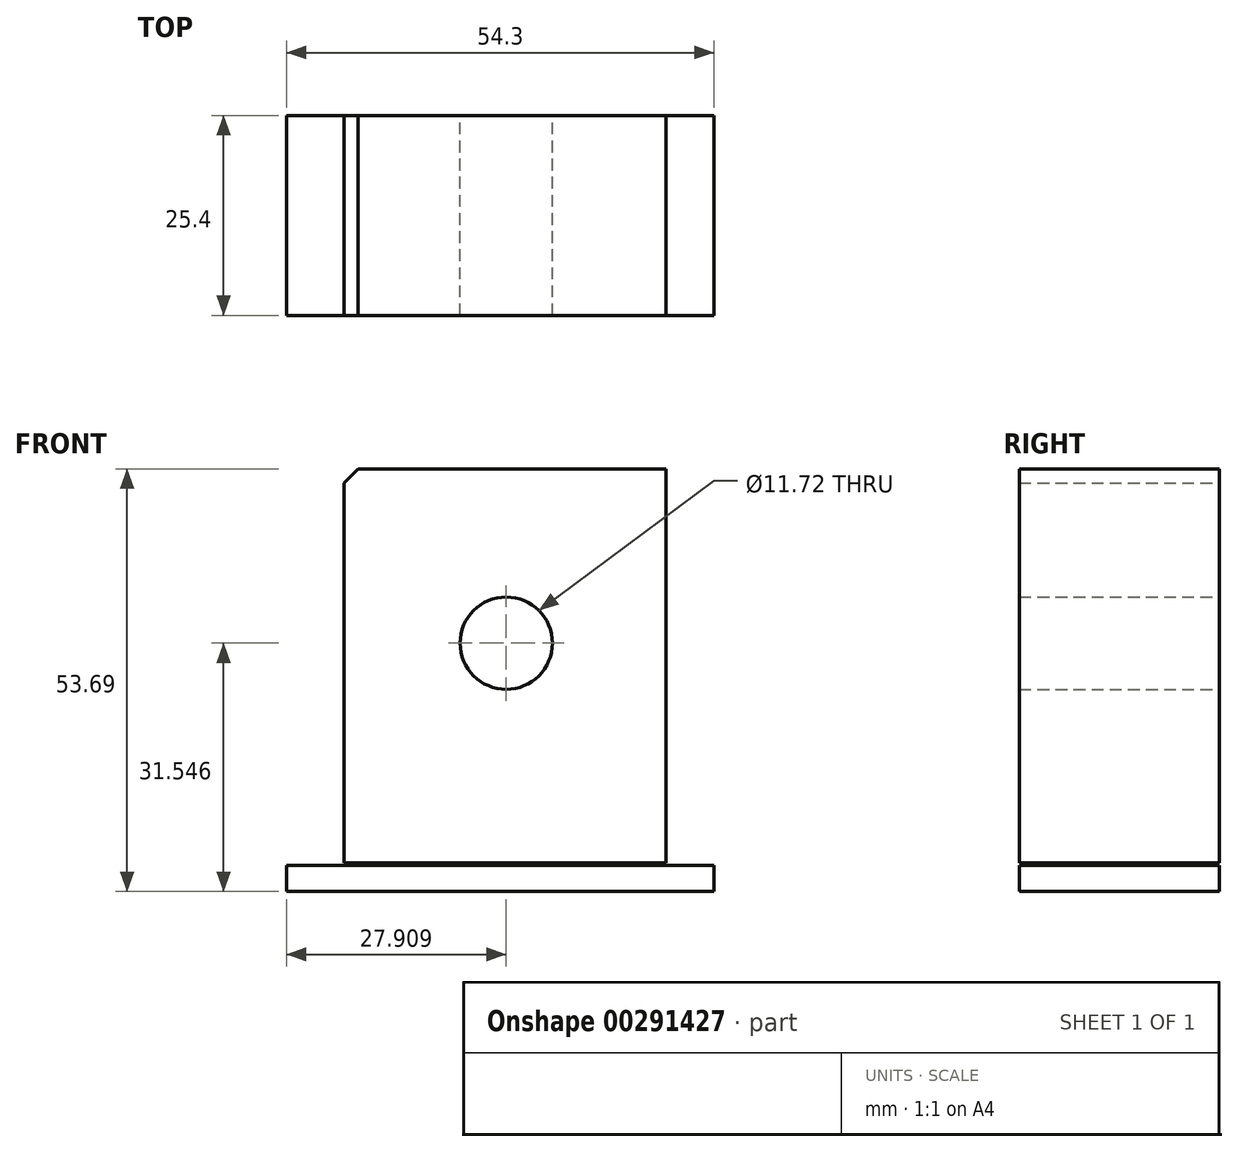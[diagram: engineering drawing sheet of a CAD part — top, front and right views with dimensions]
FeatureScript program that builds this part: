
annotation { "Feature Type Name" : "Feature", "Feature Type Description" : "" }
export const myFeature = defineFeature(function(context is Context, id is Id, definition is map)
    precondition{}
    {
        {
            var Q0;
            Q0=qCreatedBy(makeId("Front.planeOp"),FACE);
            var sketch = newSketch(context, id + "F0", { "sketchPlane" : qUnion([Q0])});
            skLineSegment(sketch, "E0.bottom", {"start": v(-24, 17.35) * mm, "end": v(16.95, 17.35) * mm});
            skLineSegment(sketch, "E0.top", {"start": v(-24, -32.7) * mm, "end": v(16.95, -32.7) * mm});
            skLineSegment(sketch, "E0.left", {"start": v(-24, 17.35) * mm, "end": v(-24, -32.7) * mm});
            skLineSegment(sketch, "E0.right", {"start": v(16.95, 17.35) * mm, "end": v(16.95, -32.7) * mm});
            skLineSegment(sketch, "E1.bottom", {"start": v(-31.28, -33) * mm, "end": v(23.02, -33) * mm});
            skLineSegment(sketch, "E1.top", {"start": v(-31.28, -36.34) * mm, "end": v(23.02, -36.34) * mm});
            skLineSegment(sketch, "E1.left", {"start": v(-31.28, -33) * mm, "end": v(-31.28, -36.34) * mm});
            skLineSegment(sketch, "E1.right", {"start": v(23.02, -33) * mm, "end": v(23.02, -36.34) * mm});
            skLineSegment(sketch, "E2", {"start": v(-39.16, 0) * mm, "end": v(0, 40.1) * mm});
            skLineSegment(sketch, "E3", {"start": v(0, 40.1) * mm, "end": v(31.2, 0) * mm});
            skCircle(sketch, "E4", {"center": v(-3.37, -4.8) * mm, "radius": 5.86 * mm});
            skCircle(sketch, "E5", {"center": v(-3.67, -25.72) * mm, "radius": 1.85 * mm});
            skSolve(sketch);
        }
        {
            var Q0;
            Q0=makeQuery(id+"F0.imprint","IMPRINT",FACE,{"disambiguationData":[TD([[makeQuery(id+"F0.imprint","IMPRINT",EDGE,{"derivedFrom":sQuery(id+"F0.wireOp",EDGE,"E1.bottom")}),-1.0]])]});
            var Q1;
            {var subQ2=sQuery(id+"F0.wireOp",EDGE,"E0.top");Q1=makeQuery(id+"F0.imprint","IMPRINT",FACE,{"disambiguationData":[TD([[makeQuery(id+"F0.imprint","IMPRINT",EDGE,{"derivedFrom":subQ2}),1.0]])]});}
            var Q2;
            Q2=makeQuery(id+"F0.imprint","IMPRINT",FACE,{"disambiguationData":[TD([[makeQuery(id+"F0.imprint","IMPRINT",EDGE,{"derivedFrom":sQuery(id+"F0.wireOp",EDGE,"E5")}),1.0]])]});
            extrude(context, id + "F1", {"entities" : qUnion([Q0, Q1, Q2]), "depth" : 25.4 * mm});
        }
    });
